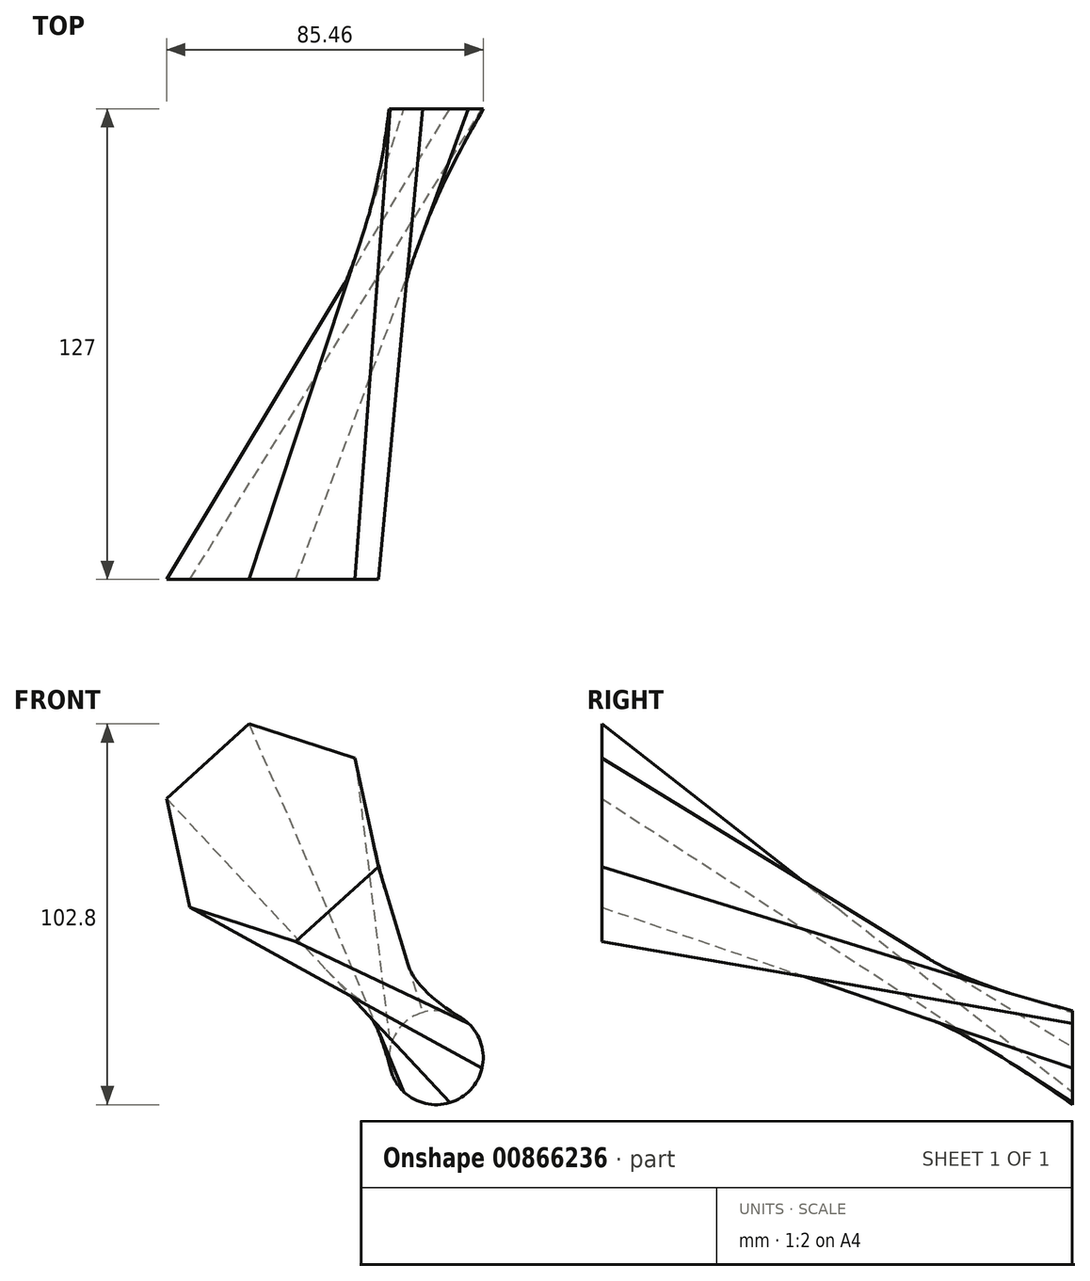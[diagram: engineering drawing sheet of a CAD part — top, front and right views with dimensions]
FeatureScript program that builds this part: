
annotation { "Feature Type Name" : "Feature", "Feature Type Description" : "" }
export const myFeature = defineFeature(function(context is Context, id is Id, definition is map)
    precondition{}
    {
        {
            var Q0;
            Q0=qCreatedBy(makeId("Front.planeOp"),FACE);
            var sketch = newSketch(context, id + "F0", { "sketchPlane" : qUnion([Q0])});
            skCircle(sketch, "E0", {"center": v(0, 0) * mm, "radius": 12.7 * mm});
            skSolve(sketch);
        }
        {
            var Q0;
            Q0=qCreatedBy(makeId("Front.planeOp"),FACE);
            cPlane(context, id + "F1", {"entities" : qUnion([Q0]), "cplaneType" : CPlaneType.OFFSET, "offset" : 127 * mm, "width" : 152.4 * mm, "height" : 152.4 * mm});
        }
        {
            var Q0;
            Q0=qCreatedBy(id+"F1.planeOp",FACE);
            var sketch = newSketch(context, id + "F2", { "sketchPlane" : qUnion([Q0])});
            skCircle(sketch, "E1.cCircle", {"center": v(-44.18, 60.73) * mm, "radius": 26.01 * mm, "construction": true});
            skLineSegment(sketch, "E1.0", {"start": v(-15.6, 51.5) * mm, "end": v(-37.9, 31.37) * mm});
            skLineSegment(sketch, "E1.1", {"start": v(-37.9, 31.37) * mm, "end": v(-66.47, 40.6) * mm});
            skLineSegment(sketch, "E1.2", {"start": v(-66.47, 40.6) * mm, "end": v(-72.76, 69.97) * mm});
            skLineSegment(sketch, "E1.3", {"start": v(-72.76, 69.97) * mm, "end": v(-50.47, 90.1) * mm});
            skLineSegment(sketch, "E1.4", {"start": v(-50.47, 90.1) * mm, "end": v(-21.9, 80.87) * mm});
            skLineSegment(sketch, "E1.5", {"start": v(-21.9, 80.87) * mm, "end": v(-15.6, 51.5) * mm});
            skPoint(sketch, "E1.0.midPoint", {"position": v(-26.75, 41.43) * mm});
            skSolve(sketch);
        }
        {
            var Q0;
            Q0 = qSketchRegion(id + "F2", true);
            var Q1;
            Q1=makeQuery(id+"F0.imprint","IMPRINT",FACE,{"disambiguationData":[TD([[makeQuery(id+"F0.imprint","IMPRINT",EDGE,{"derivedFrom":sQuery(id+"F0.wireOp",EDGE,"E0")}),1.0]])]});
            loft(context, id + "F3", {"sheetProfilesArray" : [{ "sheetProfileEntities" : qUnion([Q0]) }, { "sheetProfileEntities" : qUnion([Q1]) }]});
        }
    });
